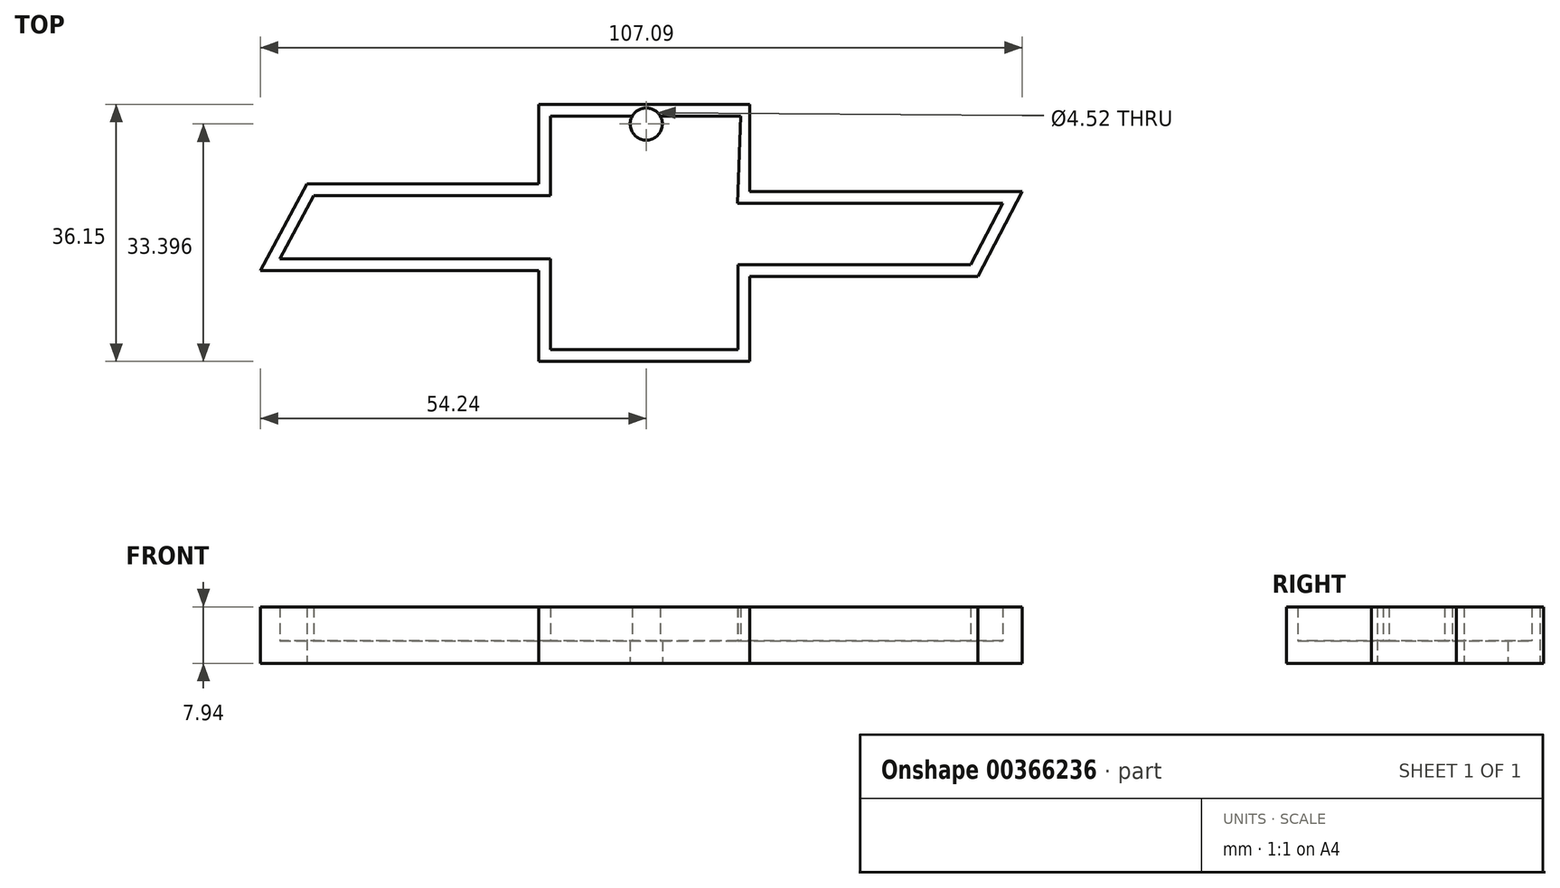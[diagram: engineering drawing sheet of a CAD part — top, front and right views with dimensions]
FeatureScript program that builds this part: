
annotation { "Feature Type Name" : "Feature", "Feature Type Description" : "" }
export const myFeature = defineFeature(function(context is Context, id is Id, definition is map)
    precondition{}
    {
        {
            var Q0;
            Q0=qCreatedBy(makeId("Top.planeOp"),FACE);
            var sketch = newSketch(context, id + "F0", { "sketchPlane" : qUnion([Q0])});
            skLineSegment(sketch, "E0", {"start": v(-15.1, 39.25) * mm, "end": v(14.53, 39.25) * mm});
            skLineSegment(sketch, "E1", {"start": v(14.53, 39.25) * mm, "end": v(14.53, 27.02) * mm});
            skLineSegment(sketch, "E2", {"start": v(-15.1, 39.25) * mm, "end": v(-15.1, 28.1) * mm});
            skLineSegment(sketch, "E3", {"start": v(-15.1, 28.1) * mm, "end": v(-47.72, 28.1) * mm});
            skLineSegment(sketch, "E4", {"start": v(-47.72, 28.1) * mm, "end": v(-54.24, 15.87) * mm});
            skLineSegment(sketch, "E5", {"start": v(-54.24, 15.87) * mm, "end": v(-15.1, 15.87) * mm});
            skLineSegment(sketch, "E6", {"start": v(14.53, 27.02) * mm, "end": v(52.85, 27.02) * mm});
            skLineSegment(sketch, "E7", {"start": v(52.85, 27.02) * mm, "end": v(46.6, 15.06) * mm});
            skLineSegment(sketch, "E8", {"start": v(46.6, 15.06) * mm, "end": v(14.53, 15.06) * mm});
            skLineSegment(sketch, "E9", {"start": v(14.53, 15.06) * mm, "end": v(14.53, 3.1) * mm});
            skLineSegment(sketch, "E10", {"start": v(14.53, 3.1) * mm, "end": v(-15.1, 3.1) * mm});
            skLineSegment(sketch, "E11", {"start": v(-15.1, 3.1) * mm, "end": v(-15.1, 15.87) * mm});
            skCircle(sketch, "E12", {"center": v(0, 36.5) * mm, "radius": 2.26 * mm});
            skSolve(sketch);
        }
        {
            var Q0;
            Q0=makeQuery(id+"F0.imprint","IMPRINT",FACE,{"disambiguationData":[TD([[makeQuery(id+"F0.imprint","IMPRINT",EDGE,{"derivedFrom":sQuery(id+"F0.wireOp",EDGE,"E0")}),-1.0]])]});
            extrude(context, id + "F1", {"entities" : qUnion([Q0]), "depth" : 3.17 * mm});
        }
        {
            var Q0;
            Q0=makeQuery(id+"F1.opExtrude","CAP_FACE",FACE,{"disambiguationData":[OSD([sQuery(id+"F0.wireOp",EDGE,"E0"),sQuery(id+"F0.wireOp",EDGE,"E1"),sQuery(id+"F0.wireOp",EDGE,"E2"),sQuery(id+"F0.wireOp",EDGE,"E3"),sQuery(id+"F0.wireOp",EDGE,"E4"),sQuery(id+"F0.wireOp",EDGE,"E5"),sQuery(id+"F0.wireOp",EDGE,"E6"),sQuery(id+"F0.wireOp",EDGE,"E7"),sQuery(id+"F0.wireOp",EDGE,"E8"),sQuery(id+"F0.wireOp",EDGE,"E9"),sQuery(id+"F0.wireOp",EDGE,"E10"),sQuery(id+"F0.wireOp",EDGE,"E11"),sQuery(id+"F0.wireOp",EDGE,"E12")])],"isStart":false});
            var sketch = newSketch(context, id + "F2", { "sketchPlane" : qUnion([Q0])});
            skLineSegment(sketch, "E13", {"start": v(-15.1, 28.1) * mm, "end": v(-15.1, 39.25) * mm});
            skLineSegment(sketch, "E14", {"start": v(-15.1, 39.25) * mm, "end": v(14.53, 39.25) * mm});
            skLineSegment(sketch, "E15", {"start": v(14.53, 27.02) * mm, "end": v(52.85, 27.02) * mm});
            skLineSegment(sketch, "E16", {"start": v(52.85, 27.02) * mm, "end": v(46.6, 15.06) * mm});
            skLineSegment(sketch, "E17", {"start": v(46.6, 15.06) * mm, "end": v(14.53, 15.06) * mm});
            skLineSegment(sketch, "E18", {"start": v(14.53, 15.06) * mm, "end": v(14.53, 3.1) * mm});
            skLineSegment(sketch, "E19", {"start": v(14.53, 3.1) * mm, "end": v(-15.1, 3.1) * mm});
            skLineSegment(sketch, "E20", {"start": v(-15.1, 3.1) * mm, "end": v(-15.1, 15.87) * mm});
            skLineSegment(sketch, "E21", {"start": v(-15.1, 15.87) * mm, "end": v(-54.24, 15.87) * mm});
            skLineSegment(sketch, "E22", {"start": v(-54.24, 15.87) * mm, "end": v(-47.72, 28.1) * mm});
            skLineSegment(sketch, "E23", {"start": v(-47.72, 28.1) * mm, "end": v(-15.1, 28.1) * mm});
            skLineSegment(sketch, "E24", {"start": v(14.94, 38.86) * mm, "end": v(14.53, 27.02) * mm});
            skLineSegment(sketch, "E25.0", {"start": v(-13.45, 26.45) * mm, "end": v(-13.45, 37.6) * mm});
            skLineSegment(sketch, "E25.1", {"start": v(45.6, 16.7) * mm, "end": v(12.87, 16.7) * mm});
            skLineSegment(sketch, "E25.2", {"start": v(50.12, 25.37) * mm, "end": v(45.6, 16.7) * mm});
            skLineSegment(sketch, "E25.3", {"start": v(12.82, 25.37) * mm, "end": v(50.12, 25.37) * mm});
            skLineSegment(sketch, "E25.4", {"start": v(13.24, 37.6) * mm, "end": v(12.82, 25.37) * mm});
            skLineSegment(sketch, "E25.5", {"start": v(12.87, 16.7) * mm, "end": v(12.87, 4.75) * mm});
            skLineSegment(sketch, "E25.6", {"start": v(-13.45, 37.6) * mm, "end": v(13.24, 37.6) * mm});
            skLineSegment(sketch, "E25.7", {"start": v(12.87, 4.75) * mm, "end": v(-13.45, 4.75) * mm});
            skLineSegment(sketch, "E25.8", {"start": v(-13.45, 4.75) * mm, "end": v(-13.45, 17.52) * mm});
            skLineSegment(sketch, "E25.9", {"start": v(-13.45, 17.52) * mm, "end": v(-51.5, 17.52) * mm});
            skLineSegment(sketch, "E25.10", {"start": v(-51.5, 17.52) * mm, "end": v(-46.73, 26.45) * mm});
            skLineSegment(sketch, "E25.11", {"start": v(-46.73, 26.45) * mm, "end": v(-13.45, 26.45) * mm});
            skSolve(sketch);
        }
        {
            var Q0;
            Q0=makeQuery(id+"F2.imprint","IMPRINT",FACE,{"disambiguationData":[TD([[makeQuery(id+"F2.imprint","IMPRINT",EDGE,{"derivedFrom":sQuery(id+"F2.wireOp",EDGE,"E13")}),1.0]])]});
            extrude(context, id + "F3", {"entities" : qUnion([Q0]), "operationType" : NewBodyOperationType.ADD, "depth" : 4.76 * mm});
        }
    });
